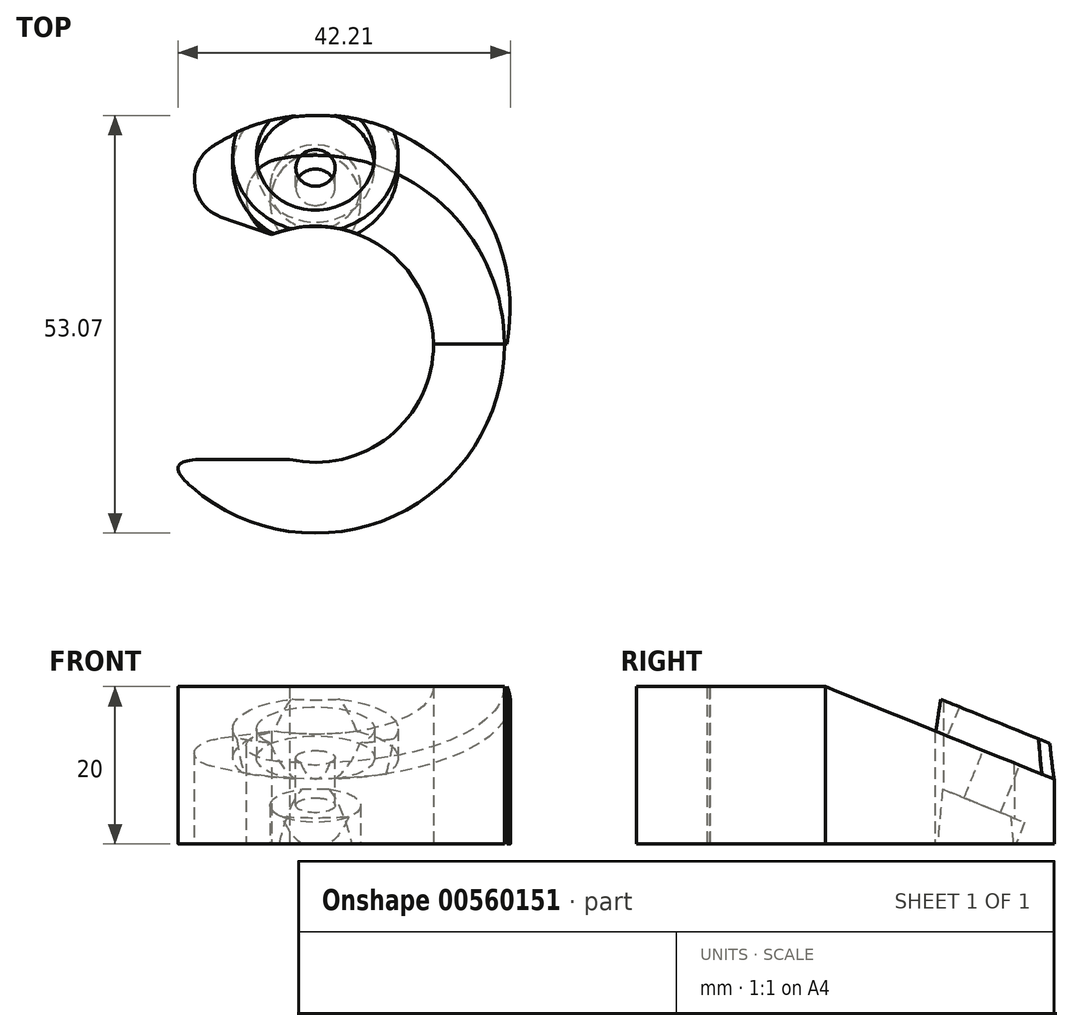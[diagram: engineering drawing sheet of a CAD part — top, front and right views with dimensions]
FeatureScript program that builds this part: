
annotation { "Feature Type Name" : "Feature", "Feature Type Description" : "" }
export const myFeature = defineFeature(function(context is Context, id is Id, definition is map)
    precondition{}
    {
        {
            var Q0;
            Q0=qCreatedBy(makeId("Top.planeOp"),FACE);
            var sketch = newSketch(context, id + "F0", { "sketchPlane" : qUnion([Q0])});
            skArc(sketch, "E0", {"start": v(24.33, 0) * mm, "mid": v(0.26, 29.07) * mm, "end": v(-23.82, 0) * mm});
            skArc(sketch, "E1", {"start": v(15, 0) * mm, "mid": v(0, 15) * mm, "end": v(-15, 0) * mm});
            skLineSegment(sketch, "E2", {"start": v(-15, 0) * mm, "end": v(-23.82, 0) * mm});
            skLineSegment(sketch, "E3", {"start": v(15, 0) * mm, "end": v(24.33, 0) * mm});
            skSolve(sketch);
        }
        {
            var Q0;
            Q0 = qSketchRegion(id + "F0", true);
            extrude(context, id + "F1", {"entities" : qUnion([Q0]), "endBound" : BoundingType.SYMMETRIC, "depth" : 20 * mm, "offsetDistance" : 25 * mm});
        }
        {
            var Q0;
            Q0=qCreatedBy(makeId("Top.planeOp"),FACE);
            var sketch = newSketch(context, id + "F2", { "sketchPlane" : qUnion([Q0])});
            skCircle(sketch, "E4", {"center": v(0, 0) * mm, "radius": 15 * mm});
            skCircle(sketch, "E5", {"center": v(0, 0) * mm, "radius": 24 * mm});
            skSolve(sketch);
        }
        {
            var Q0;
            Q0 = qSketchRegion(id + "F2", true);
            extrude(context, id + "F3", {"entities" : qUnion([Q0]), "endBound" : BoundingType.SYMMETRIC, "depth" : 20 * mm, "offsetDistance" : 25 * mm});
        }
        {
            var Q0;
            Q0=qCreatedBy(makeId("Top.planeOp"),FACE);
            var sketch = newSketch(context, id + "F4", { "sketchPlane" : qUnion([Q0])});
            skLineSegment(sketch, "E6", {"start": v(-5.1, 13.78) * mm, "end": v(-14.95, -14.56) * mm});
            skLineSegment(sketch, "E7", {"start": v(-14.95, -14.56) * mm, "end": v(-34.78, -7.67) * mm});
            skLineSegment(sketch, "E8", {"start": v(-34.78, -7.67) * mm, "end": v(-24.94, 20.67) * mm});
            skLineSegment(sketch, "E9", {"start": v(-24.94, 20.67) * mm, "end": v(-5.1, 13.78) * mm});
            skSolve(sketch);
        }
        {
            var Q0;
            Q0 = qSketchRegion(id + "F4", true);
            extrude(context, id + "F5", {"entities" : qUnion([Q0]), "endBound" : BoundingType.SYMMETRIC, "depth" : 25 * mm, "offsetDistance" : 25 * mm});
        }
        {
            var Q0;
            Q0=qCreatedBy(makeId("Top.planeOp"),FACE);
            var sketch = newSketch(context, id + "F6", { "sketchPlane" : qUnion([Q0])});
            skLineSegment(sketch, "E10.bottom", {"start": v(-24.13, -14.64) * mm, "end": v(-1.71, -14.64) * mm});
            skLineSegment(sketch, "E10.top", {"start": v(-24.13, -4.44) * mm, "end": v(-1.71, -4.44) * mm});
            skLineSegment(sketch, "E10.left", {"start": v(-24.13, -14.64) * mm, "end": v(-24.13, -4.44) * mm});
            skLineSegment(sketch, "E10.right", {"start": v(-1.71, -14.64) * mm, "end": v(-1.71, -4.44) * mm});
            skSolve(sketch);
        }
        {
            var Q0;
            Q0 = qSketchRegion(id + "F6", true);
            extrude(context, id + "F7", {"entities" : qUnion([Q0]), "endBound" : BoundingType.SYMMETRIC, "depth" : 25 * mm, "offsetDistance" : 25 * mm});
        }
        {
            var Q0;
            Q0=makeQuery(id+"F5.opExtrude","SWEPT_BODY",BODY,{"disambiguationData":[OSD([sQuery(id+"F4.wireOp",EDGE,"E6"),sQuery(id+"F4.wireOp",EDGE,"E7"),sQuery(id+"F4.wireOp",EDGE,"E8"),sQuery(id+"F4.wireOp",EDGE,"E9")])]});
            var Q1;
            Q1=makeQuery(id+"F7.opExtrude","SWEPT_BODY",BODY,{"disambiguationData":[OSD([sQuery(id+"F6.wireOp",EDGE,"E10.bottom"),sQuery(id+"F6.wireOp",EDGE,"E10.top"),sQuery(id+"F6.wireOp",EDGE,"E10.left"),sQuery(id+"F6.wireOp",EDGE,"E10.right")])]});
            var Q2;
            Q2=makeQuery(id+"F1.opExtrude","SWEPT_BODY",BODY,{"disambiguationData":[OSD([sQuery(id+"F0.wireOp",EDGE,"E0"),sQuery(id+"F0.wireOp",EDGE,"E1"),sQuery(id+"F0.wireOp",EDGE,"E2"),sQuery(id+"F0.wireOp",EDGE,"E3")])]});
            var Q3;
            Q3=makeQuery(id+"F3.opExtrude","SWEPT_BODY",BODY,{"disambiguationData":[OSD([sQuery(id+"F2.wireOp",EDGE,"E4"),sQuery(id+"F2.wireOp",EDGE,"E5")])]});
            booleanBodies(context, id + "F8", {"operationType" : BooleanOperationType.SUBTRACTION, "tools" : qUnion([Q0, Q1]), "targets" : qUnion([Q2, Q3])});
        }
        {
            var Q0;
            Q0=makeQuery(id+"F3.opExtrude","CAP_FACE",FACE,{"disambiguationData":[OSD([sQuery(id+"F2.wireOp",EDGE,"E4"),sQuery(id+"F2.wireOp",EDGE,"E5")])],"isStart":false});
            cPlane(context, id + "F9", {"entities" : qUnion([Q0]), "cplaneType" : CPlaneType.OFFSET, "offset" : 0 * mm, "width" : 150 * mm, "height" : 150 * mm});
        }
        {
            var Q0;
            Q0=qCreatedBy(id+"F9.planeOp",FACE);
            var sketch = newSketch(context, id + "F10", { "sketchPlane" : qUnion([Q0])});
            skLineSegment(sketch, "E11", {"start": v(-16.49, 0) * mm, "end": v(42.9, 0) * mm});
            skSolve(sketch);
        }
        {
            var Q0;
            Q0 = qBodyType(qCreatedBy(id + "F10" ,EDGE), BodyType.WIRE);
            cPlane(context, id + "F11", {"entities" : qUnion([Q0]), "cplaneType" : CPlaneType.LINE_ANGLE, "offset" : 25 * mm, "angle" : 68 * degree, "width" : 150 * mm, "height" : 150 * mm});
        }
        {
            var Q0;
            Q0=qCreatedBy(id+"F11.planeOp",FACE);
            var sketch = newSketch(context, id + "F12", { "sketchPlane" : qUnion([Q0])});
            skLineSegment(sketch, "E12.bottom", {"start": v(27.66, -3.88) * mm, "end": v(-24.07, -3.88) * mm});
            skLineSegment(sketch, "E12.top", {"start": v(27.66, 31.47) * mm, "end": v(-24.07, 31.47) * mm});
            skLineSegment(sketch, "E12.left", {"start": v(27.66, -3.88) * mm, "end": v(27.66, 31.47) * mm});
            skLineSegment(sketch, "E12.right", {"start": v(-24.07, -3.88) * mm, "end": v(-24.07, 31.47) * mm});
            skSolve(sketch);
        }
        {
            var Q0;
            Q0 = qSketchRegion(id + "F12", true);
            extrude(context, id + "F13", {"entities" : qUnion([Q0]), "depth" : 25 * mm, "offsetDistance" : 25 * mm});
        }
        {
            var Q0;
            Q0=makeQuery(id+"F13.opExtrude","SWEPT_BODY",BODY,{"disambiguationData":[OSD([sQuery(id+"F12.wireOp",EDGE,"E12.bottom"),sQuery(id+"F12.wireOp",EDGE,"E12.top"),sQuery(id+"F12.wireOp",EDGE,"E12.left"),sQuery(id+"F12.wireOp",EDGE,"E12.right")])]});
            var Q1;
            Q1=makeQuery(id+"F3.opExtrude","SWEPT_BODY",BODY,{"disambiguationData":[OSD([sQuery(id+"F2.wireOp",EDGE,"E4"),sQuery(id+"F2.wireOp",EDGE,"E5")])]});
            var Q2;
            Q2=makeQuery(id+"F1.opExtrude","SWEPT_BODY",BODY,{"disambiguationData":[OSD([sQuery(id+"F0.wireOp",EDGE,"E0"),sQuery(id+"F0.wireOp",EDGE,"E1"),sQuery(id+"F0.wireOp",EDGE,"E2"),sQuery(id+"F0.wireOp",EDGE,"E3")])]});
            booleanBodies(context, id + "F14", {"operationType" : BooleanOperationType.SUBTRACTION, "tools" : qUnion([Q0]), "targets" : qUnion([Q1, Q2])});
        }
        {
            var Q0;
            {var subQ0=sQuery(id+"F0.wireOp",EDGE,"E0");var subQ1=makeQuery(id+"F1.opExtrude","SWEPT_FACE",FACE,{"disambiguationData":[OSD([subQ0])]});Q0=makeQuery(id+"F14.opBoolean","COPY",FACE,{"disambiguationData":[TD([subQ1])],"derivedFrom":makeQuery(id+"F13.opExtrude","CAP_FACE",FACE,{"disambiguationData":[OSD([sQuery(id+"F12.wireOp",EDGE,"E12.bottom"),sQuery(id+"F12.wireOp",EDGE,"E12.top"),sQuery(id+"F12.wireOp",EDGE,"E12.left"),sQuery(id+"F12.wireOp",EDGE,"E12.right")])],"isStart":true})});}
            var sketch = newSketch(context, id + "F15", { "sketchPlane" : qUnion([Q0])});
            skCircle(sketch, "E13", {"center": v(0, 20.4) * mm, "radius": 2.5 * mm});
            skSolve(sketch);
        }
        {
            var Q0;
            Q0 = qSketchRegion(id + "F15", true);
            extrude(context, id + "F16", {"entities" : qUnion([Q0]), "oppositeDirection" : true, "depth" : 15 * mm, "offsetDistance" : 25 * mm});
        }
        {
            var Q0;
            {var subQ0=sQuery(id+"F0.wireOp",EDGE,"E0");var subQ1=makeQuery(id+"F1.opExtrude","SWEPT_FACE",FACE,{"disambiguationData":[OSD([subQ0])]});Q0=makeQuery(id+"F14.opBoolean","COPY",FACE,{"disambiguationData":[TD([subQ1])],"derivedFrom":makeQuery(id+"F13.opExtrude","CAP_FACE",FACE,{"disambiguationData":[OSD([sQuery(id+"F12.wireOp",EDGE,"E12.bottom"),sQuery(id+"F12.wireOp",EDGE,"E12.top"),sQuery(id+"F12.wireOp",EDGE,"E12.left"),sQuery(id+"F12.wireOp",EDGE,"E12.right")])],"isStart":true})});}
            var sketch = newSketch(context, id + "F17", { "sketchPlane" : qUnion([Q0])});
            skCircle(sketch, "E14", {"center": v(0, 20.48) * mm, "radius": 7.5 * mm});
            skCircle(sketch, "E15", {"center": v(0, 20.48) * mm, "radius": 10.5 * mm});
            skSolve(sketch);
        }
        {
            var Q0;
            Q0 = qSketchRegion(id + "F17", true);
            extrude(context, id + "F18", {"entities" : qUnion([Q0]), "depth" : 4 * mm, "offsetDistance" : 25 * mm});
        }
        {
            var Q0;
            Q0=qCreatedBy(makeId("Top.planeOp"),FACE);
            var sketch = newSketch(context, id + "F19", { "sketchPlane" : qUnion([Q0])});
            skLineSegment(sketch, "E16.top", {"start": v(-31.52, -6.66) * mm, "end": v(15.78, -6.66) * mm});
            skArc(sketch, "E17", {"start": v(15, 0) * mm, "mid": v(0, 15) * mm, "end": v(-15, 0) * mm});
            skArc(sketch, "E18", {"start": v(24.17, 0) * mm, "mid": v(0.16, 29.16) * mm, "end": v(-23.85, 0) * mm});
            skLineSegment(sketch, "E19", {"start": v(24.17, 0) * mm, "end": v(15, 0) * mm});
            skLineSegment(sketch, "E20", {"start": v(-23.85, 0) * mm, "end": v(-15, 0) * mm});
            skLineSegment(sketch, "E21.bottom", {"start": v(29.66, -4.32) * mm, "end": v(-31.6, -4.32) * mm});
            skLineSegment(sketch, "E21.top", {"start": v(29.66, 40.47) * mm, "end": v(-31.6, 40.47) * mm});
            skLineSegment(sketch, "E21.left", {"start": v(29.66, -4.32) * mm, "end": v(29.66, 40.47) * mm});
            skLineSegment(sketch, "E21.right", {"start": v(-31.6, -4.32) * mm, "end": v(-31.6, 40.47) * mm});
            skSolve(sketch);
        }
        {
            var Q0;
            Q0 = qSketchRegion(id + "F19", true);
            extrude(context, id + "F20", {"entities" : qUnion([Q0]), "endBound" : BoundingType.SYMMETRIC, "depth" : 25 * mm, "offsetDistance" : 25 * mm});
        }
        {
            var Q0;
            Q0=makeQuery(id+"F20.opExtrude","SWEPT_BODY",BODY,{"disambiguationData":[OSD([sQuery(id+"F19.wireOp",EDGE,"E17"),sQuery(id+"F19.wireOp",EDGE,"E18"),sQuery(id+"F19.wireOp",EDGE,"E19"),sQuery(id+"F19.wireOp",EDGE,"E20"),sQuery(id+"F19.wireOp",EDGE,"E21.bottom"),sQuery(id+"F19.wireOp",EDGE,"E21.top"),sQuery(id+"F19.wireOp",EDGE,"E21.left"),sQuery(id+"F19.wireOp",EDGE,"E21.right")])]});
            var Q1;
            Q1=makeQuery(id+"F18.opExtrude","SWEPT_BODY",BODY,{"disambiguationData":[OSD([sQuery(id+"F17.wireOp",EDGE,"E14"),sQuery(id+"F17.wireOp",EDGE,"E15")])]});
            booleanBodies(context, id + "F21", {"operationType" : BooleanOperationType.SUBTRACTION, "tools" : qUnion([Q0]), "targets" : qUnion([Q1])});
        }
        {
            var Q0;
            Q0=makeQuery(id+"F16.opExtrude","SWEPT_BODY",BODY,{"disambiguationData":[OSD([sQuery(id+"F15.wireOp",EDGE,"E13")])]});
            var Q1;
            Q1=makeQuery(id+"F1.opExtrude","SWEPT_BODY",BODY,{"disambiguationData":[OSD([sQuery(id+"F0.wireOp",EDGE,"E0"),sQuery(id+"F0.wireOp",EDGE,"E1"),sQuery(id+"F0.wireOp",EDGE,"E2"),sQuery(id+"F0.wireOp",EDGE,"E3")])]});
            var Q2;
            Q2=makeQuery(id+"F3.opExtrude","SWEPT_BODY",BODY,{"disambiguationData":[OSD([sQuery(id+"F2.wireOp",EDGE,"E4"),sQuery(id+"F2.wireOp",EDGE,"E5")])]});
            booleanBodies(context, id + "F22", {"operationType" : BooleanOperationType.SUBTRACTION, "tools" : qUnion([Q0]), "targets" : qUnion([Q1, Q2])});
        }
        {
            var Q0;
            Q0=makeQuery(id+"F8.opBoolean","INTERSECT",EDGE,{"derivedFrom":[makeQuery(id+"F1.opExtrude","SWEPT_FACE",FACE,{"disambiguationData":[OSD([sQuery(id+"F0.wireOp",EDGE,"E0")])]}),makeQuery(id+"F5.opExtrude","SWEPT_FACE",FACE,{"disambiguationData":[OSD([sQuery(id+"F4.wireOp",EDGE,"E9")])]})]});
            var Q1;
            Q1=makeQuery(id+"F8.opBoolean","INTERSECT",EDGE,{"derivedFrom":[makeQuery(id+"F3.opExtrude","SWEPT_FACE",FACE,{"disambiguationData":[OSD([sQuery(id+"F2.wireOp",EDGE,"E5")])]}),makeQuery(id+"F5.opExtrude","SWEPT_FACE",FACE,{"disambiguationData":[OSD([sQuery(id+"F4.wireOp",EDGE,"E9")])]})]});
            fillet(context, id + "F23", {"entities" : qUnion([Q0, Q1]), "radius" : 5 * mm, "tangentPropagation" : true, "allowEdgeOverflow" : false});
        }
        {
            var Q0;
            Q0=makeQuery(id+"F8.opBoolean","INTERSECT",EDGE,{"derivedFrom":[makeQuery(id+"F3.opExtrude","SWEPT_FACE",FACE,{"disambiguationData":[OSD([sQuery(id+"F2.wireOp",EDGE,"E5")])]}),makeQuery(id+"F7.opExtrude","SWEPT_FACE",FACE,{"disambiguationData":[OSD([sQuery(id+"F6.wireOp",EDGE,"E10.bottom")])]})]});
            fillet(context, id + "F24", {"entities" : qUnion([Q0]), "radius" : 2 * mm, "tangentPropagation" : true, "rho" : 0.5, "crossSection" : FilletCrossSection.CONIC, "allowEdgeOverflow" : false});
        }
        {
            var Q0;
            {var subQ0=sQuery(id+"F0.wireOp",EDGE,"E0");var subQ1=makeQuery(id+"F1.opExtrude","SWEPT_FACE",FACE,{"disambiguationData":[OSD([subQ0])]});Q0=makeQuery(id+"F14.opBoolean","COPY",FACE,{"disambiguationData":[TD([subQ1])],"derivedFrom":makeQuery(id+"F13.opExtrude","CAP_FACE",FACE,{"disambiguationData":[OSD([sQuery(id+"F12.wireOp",EDGE,"E12.bottom"),sQuery(id+"F12.wireOp",EDGE,"E12.top"),sQuery(id+"F12.wireOp",EDGE,"E12.left"),sQuery(id+"F12.wireOp",EDGE,"E12.right")])],"isStart":true})});}
            cPlane(context, id + "F25", {"entities" : qUnion([Q0]), "cplaneType" : CPlaneType.OFFSET, "offset" : 10 * mm, "oppositeDirection" : true, "width" : 150 * mm, "height" : 150 * mm});
        }
        {
            var Q0;
            Q0=qCreatedBy(id+"F25.planeOp",FACE);
            var sketch = newSketch(context, id + "F26", { "sketchPlane" : qUnion([Q0])});
            skPoint(sketch, "E22.0.midPoint", {"position": v(0, 23.83) * mm});
            skCircle(sketch, "E23", {"center": v(0, 20.44) * mm, "radius": 5.75 * mm});
            skSolve(sketch);
        }
        {
            var Q0;
            Q0 = qSketchRegion(id + "F26", true);
            extrude(context, id + "F27", {"entities" : qUnion([Q0]), "endBound" : BoundingType.SYMMETRIC, "depth" : 7 * mm, "offsetDistance" : 25 * mm});
        }
        {
            var Q0;
            Q0=makeQuery(id+"F27.opExtrude","SWEPT_BODY",BODY,{"disambiguationData":[OSD([sQuery(id+"F26.wireOp",EDGE,"E23")])]});
            var Q1;
            Q1=makeQuery(id+"F1.opExtrude","SWEPT_BODY",BODY,{"disambiguationData":[OSD([sQuery(id+"F0.wireOp",EDGE,"E0"),sQuery(id+"F0.wireOp",EDGE,"E1"),sQuery(id+"F0.wireOp",EDGE,"E2"),sQuery(id+"F0.wireOp",EDGE,"E3")])]});
            var Q2;
            Q2=makeQuery(id+"F3.opExtrude","SWEPT_BODY",BODY,{"disambiguationData":[OSD([sQuery(id+"F2.wireOp",EDGE,"E4"),sQuery(id+"F2.wireOp",EDGE,"E5")])]});
            booleanBodies(context, id + "F28", {"operationType" : BooleanOperationType.SUBTRACTION, "tools" : qUnion([Q0]), "targets" : qUnion([Q1, Q2])});
        }
    });
